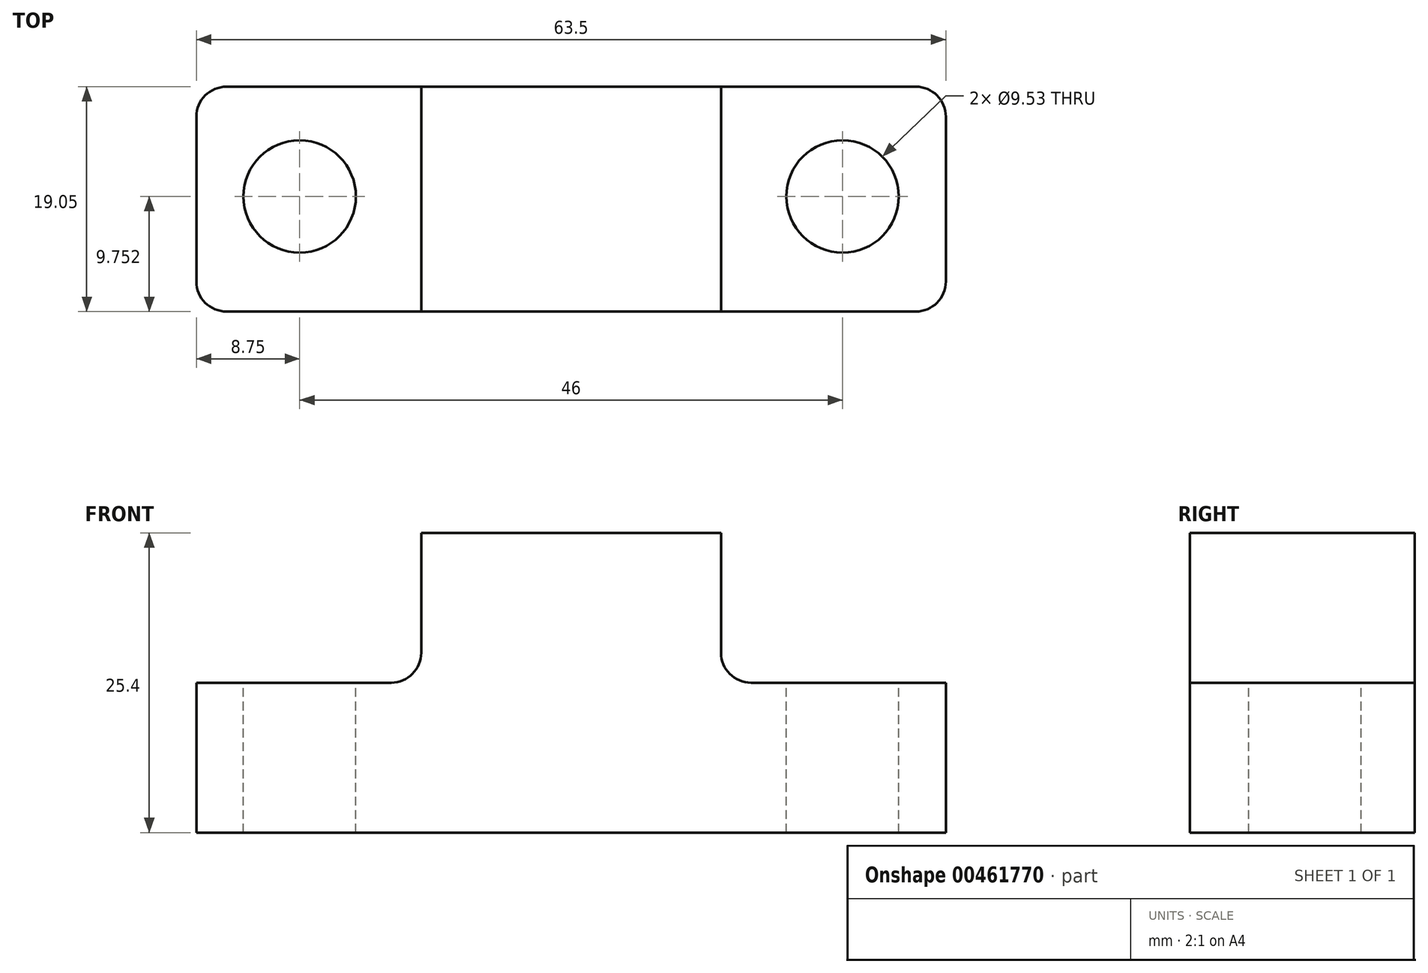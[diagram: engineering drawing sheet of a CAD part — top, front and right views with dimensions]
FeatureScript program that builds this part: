
annotation { "Feature Type Name" : "Feature", "Feature Type Description" : "" }
export const myFeature = defineFeature(function(context is Context, id is Id, definition is map)
    precondition{}
    {
        {
            var Q0;
            Q0=qCreatedBy(makeId("Front.planeOp"),FACE);
            var sketch = newSketch(context, id + "F0", { "sketchPlane" : qUnion([Q0])});
            skLineSegment(sketch, "E0", {"start": v(0, 0) * mm, "end": v(-31.75, 0) * mm});
            skLineSegment(sketch, "E1", {"start": v(-31.75, 0) * mm, "end": v(-31.75, 12.7) * mm});
            skLineSegment(sketch, "E2", {"start": v(-31.75, 12.7) * mm, "end": v(-12.7, 12.7) * mm});
            skLineSegment(sketch, "E3", {"start": v(-12.7, 12.7) * mm, "end": v(-12.7, 25.4) * mm});
            skLineSegment(sketch, "E4", {"start": v(-12.7, 25.4) * mm, "end": v(0, 25.4) * mm});
            skLineSegment(sketch, "E5", {"start": v(0, 25.4) * mm, "end": v(0, 0) * mm});
            skSolve(sketch);
        }
        {
            var Q0;
            Q0=makeQuery(id+"F0.imprint","IMPRINT",FACE,{"disambiguationData":[TD([[makeQuery(id+"F0.imprint","IMPRINT",EDGE,{"derivedFrom":sQuery(id+"F0.wireOp",EDGE,"E0")}),-1.0]])]});
            extrude(context, id + "F1", {"entities" : qUnion([Q0]), "depth" : 19.05 * mm});
        }
        {
            var Q0;
            Q0=makeQuery(id+"F1.opExtrude","SWEPT_BODY",BODY,{"disambiguationData":[OSD([sQuery(id+"F0.wireOp",EDGE,"E0"),sQuery(id+"F0.wireOp",EDGE,"E1"),sQuery(id+"F0.wireOp",EDGE,"E2"),sQuery(id+"F0.wireOp",EDGE,"E3"),sQuery(id+"F0.wireOp",EDGE,"E4"),sQuery(id+"F0.wireOp",EDGE,"E5")])]});
            var Q1;
            Q1=makeQuery(id+"F1.opExtrude","SWEPT_FACE",FACE,{"disambiguationData":[OSD([sQuery(id+"F0.wireOp",EDGE,"E5")])]});
            mirror(context, id + "F2", {"operationType" : NewBodyOperationType.ADD, "entities" : qUnion([Q0]), "mirrorPlane" : qUnion([Q1])});
        }
        {
            var Q0;
            Q0=makeQuery(id+"F1.opExtrude","CAP_EDGE",EDGE,{"disambiguationData":[OSD([sQuery(id+"F0.wireOp",EDGE,"E1")])],"isStart":false});
            var Q1;
            Q1=makeQuery(id+"F1.opExtrude","CAP_EDGE",EDGE,{"disambiguationData":[OSD([sQuery(id+"F0.wireOp",EDGE,"E1")])],"isStart":true});
            var Q2;
            Q2=makeQuery(id+"F2.opPattern","COPY",EDGE,{"derivedFrom":makeQuery(id+"F1.opExtrude","CAP_EDGE",EDGE,{"disambiguationData":[OSD([sQuery(id+"F0.wireOp",EDGE,"E1")])],"isStart":false}),"instanceName":"1"});
            var Q3;
            Q3=makeQuery(id+"F2.opPattern","COPY",EDGE,{"derivedFrom":makeQuery(id+"F1.opExtrude","CAP_EDGE",EDGE,{"disambiguationData":[OSD([sQuery(id+"F0.wireOp",EDGE,"E1")])],"isStart":true}),"instanceName":"1"});
            var Q4;
            Q4=makeQuery(id+"F2.opPattern","COPY",EDGE,{"derivedFrom":makeQuery(id+"F1.opExtrude","SWEPT_EDGE",EDGE,{"disambiguationData":[OSD([sQuery(id+"F0.wireOp",EDGE,"E2"),sQuery(id+"F0.wireOp",EDGE,"E3")])]}),"instanceName":"1"});
            var Q5;
            Q5=makeQuery(id+"F1.opExtrude","SWEPT_EDGE",EDGE,{"disambiguationData":[OSD([sQuery(id+"F0.wireOp",EDGE,"E2"),sQuery(id+"F0.wireOp",EDGE,"E3")])]});
            fillet(context, id + "F3", {"entities" : qUnion([Q0, Q1, Q2, Q3, Q4, Q5]), "radius" : 2.54 * mm, "tangentPropagation" : true, "allowEdgeOverflow" : false});
        }
        {
            var Q0;
            Q0=qCreatedBy(makeId("Top.planeOp"),FACE);
            cPlane(context, id + "F4", {"entities" : qUnion([Q0]), "cplaneType" : CPlaneType.OFFSET, "offset" : 12.95 * mm, "width" : 152.4 * mm, "height" : 152.4 * mm});
        }
        {
            var Q0;
            Q0=qCreatedBy(id+"F4.planeOp",FACE);
            var sketch = newSketch(context, id + "F5", { "sketchPlane" : qUnion([Q0])});
            skPoint(sketch, "E6", {"position": v(-23, -9.3) * mm});
            skPoint(sketch, "E7", {"position": v(23, -9.3) * mm});
            skCircle(sketch, "E8", {"center": v(-23, -9.3) * mm, "radius": 4.76 * mm});
            skCircle(sketch, "E9", {"center": v(23, -9.3) * mm, "radius": 4.76 * mm});
            skSolve(sketch);
        }
        {
            var Q0;
            Q0=sQuery(id+"F5.wireOp",VERTEX,"E6");
            var Q1;
            Q1=sQuery(id+"F5.wireOp",VERTEX,"E7");
            var Q2;
            Q2=makeQuery(id+"F1.opExtrude","SWEPT_BODY",BODY,{"disambiguationData":[OSD([sQuery(id+"F0.wireOp",EDGE,"E0"),sQuery(id+"F0.wireOp",EDGE,"E1"),sQuery(id+"F0.wireOp",EDGE,"E2"),sQuery(id+"F0.wireOp",EDGE,"E3"),sQuery(id+"F0.wireOp",EDGE,"E4"),sQuery(id+"F0.wireOp",EDGE,"E5")])]});
            hole(context, id + "F6", {"style" : HoleStyle.SIMPLE, "endStyle" : HoleEndStyle.THROUGH, "holeDiameter" : 9.52 * mm, "isTappedThrough" : true, "tappedDepth" : 12.7 * mm, "tapClearance" : 3, "locations" : qUnion([Q0, Q1]), "scope" : qUnion([Q2])});
        }
    });
